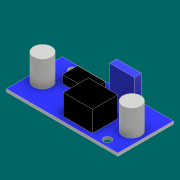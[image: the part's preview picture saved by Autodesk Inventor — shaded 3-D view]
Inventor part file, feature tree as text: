
AUTODESK INVENTOR PART (.ipt)
format: ipt  version: 2017.3 (Build 213257000, 257)  size: 138,240 bytes
history: native  units: mm
features: extrude x6, sketch x6
ambient origin geometry x8: Origin, YZ Plane, XZ Plane, XY Plane, X Axis, Y Axis, Z Axis, Center Point
bodies: Solid1 (feature_tree)
feature tree (12):
  extrude  "Extrusion1"  Depth=21.5mm
  extrude  "Extrusion2"  Depth=1.1mm TaperAngle=0.0deg
  extrude  "Extrusion3"  Depth=2.5mm
  extrude  "Extrusion4"  Depth=3.0mm
  extrude  "Extrusion5"  Depth=3.0mm
  extrude  "Extrusion6"  Depth=7.0mm
  sketch  "Sketch1"  dims[d0=43.0mm d1=21.5mm]
  sketch  "Sketch2"  dims[d2=43.0mm d3=1.1mm d4=0.0mm]
  sketch  "Sketch3"  dims[d5=6.5mm d6=2.5mm]
  sketch  "Sketch4"  dims[d7=3.0mm d8=6.5mm]
  sketch  "Sketch5"  dims[d9=2.5mm d10=3.0mm]
  sketch  "Sketch6"  dims[d11=1.1mm d12=0.0mm d13=7.0mm d14=7.0mm d15=10.0mm d16=0.0mm d17=11.0mm d18=0.0mm d19=8.0mm d20=0.0mm d21=3.0mm d22=0.0mm]
